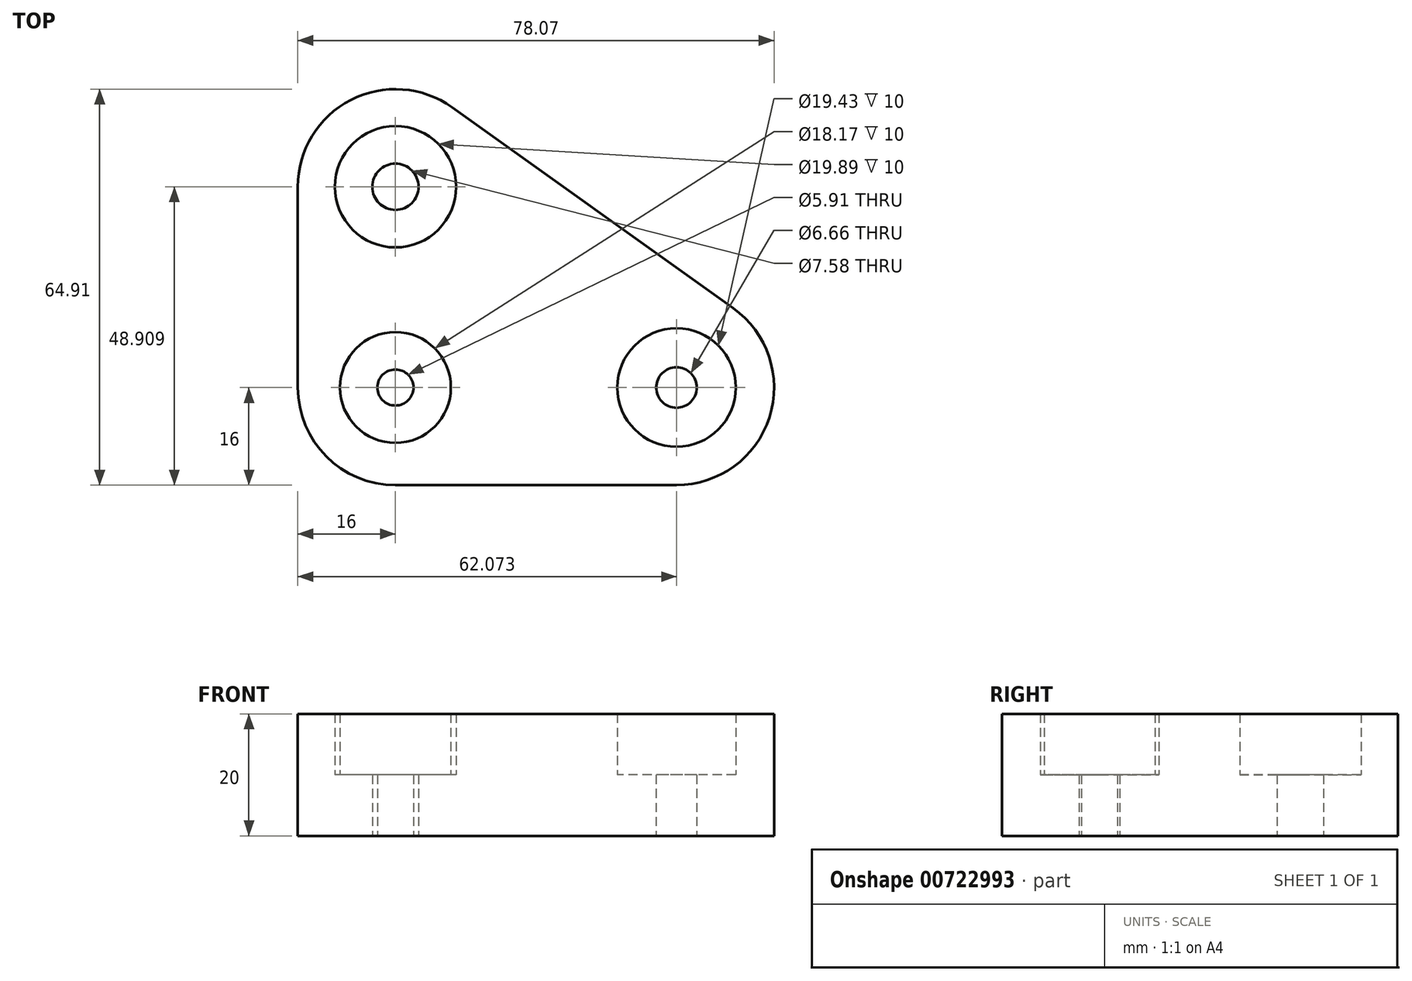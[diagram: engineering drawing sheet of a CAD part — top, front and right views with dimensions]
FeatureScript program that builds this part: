
annotation { "Feature Type Name" : "Feature", "Feature Type Description" : "" }
export const myFeature = defineFeature(function(context is Context, id is Id, definition is map)
    precondition{}
    {
        {
            var Q0;
            Q0=qCreatedBy(makeId("Top.planeOp"),FACE);
            var sketch = newSketch(context, id + "F0", { "sketchPlane" : qUnion([Q0])});
            skLineSegment(sketch, "E0.bottom", {"start": v(16, 0) * mm, "end": v(62.07, 0) * mm});
            skLineSegment(sketch, "E0.left", {"start": v(0, 16) * mm, "end": v(0, 48.9) * mm});
            skLineSegment(sketch, "E1", {"start": v(25.3, 61.93) * mm, "end": v(71.37, 29.02) * mm});
            skPoint(sketch, "E2.visualSharp", {"position": v(0, 0) * mm});
            skArc(sketch, "E2.filletArc", {"start": v(0, 16) * mm, "mid": v(4.69, 4.69) * mm, "end": v(16, 0) * mm});
            skPoint(sketch, "E3.visualSharp", {"position": v(0, 80) * mm});
            skArc(sketch, "E3.filletArc", {"start": v(25.3, 61.93) * mm, "mid": v(8.68, 63.14) * mm, "end": v(0, 48.9) * mm});
            skPoint(sketch, "E4.visualSharp", {"position": v(112, 0) * mm});
            skArc(sketch, "E4.filletArc", {"start": v(62.07, 0) * mm, "mid": v(77.3, 11.12) * mm, "end": v(71.37, 29.02) * mm});
            skCircle(sketch, "E5", {"center": v(16, 16) * mm, "radius": 9.09 * mm});
            skCircle(sketch, "E6", {"center": v(62.07, 16) * mm, "radius": 9.71 * mm});
            skCircle(sketch, "E7", {"center": v(16, 16) * mm, "radius": 2.96 * mm});
            skCircle(sketch, "E8", {"center": v(62.07, 16) * mm, "radius": 3.33 * mm});
            skCircle(sketch, "E9", {"center": v(16, 48.9) * mm, "radius": 9.94 * mm});
            skCircle(sketch, "E10", {"center": v(16, 48.9) * mm, "radius": 3.8 * mm});
            skSolve(sketch);
        }
        {
            var Q0;
            Q0 = qSketchRegion(id + "F0", true);
            extrude(context, id + "F1", {"entities" : qUnion([Q0]), "depth" : 20 * mm, "offsetDistance" : 25 * mm});
        }
        {
            var Q0;
            Q0=makeQuery(id+"F0.imprint","IMPRINT",FACE,{"disambiguationData":[TD([[makeQuery(id+"F0.imprint","IMPRINT",EDGE,{"derivedFrom":sQuery(id+"F0.wireOp",EDGE,"E5")}),1.0]])]});
            var Q1;
            Q1=makeQuery(id+"F0.imprint","IMPRINT",FACE,{"disambiguationData":[TD([[makeQuery(id+"F0.imprint","IMPRINT",EDGE,{"derivedFrom":sQuery(id+"F0.wireOp",EDGE,"E9")}),1.0]])]});
            var Q2;
            Q2=makeQuery(id+"F0.imprint","IMPRINT",FACE,{"disambiguationData":[TD([[makeQuery(id+"F0.imprint","IMPRINT",EDGE,{"derivedFrom":sQuery(id+"F0.wireOp",EDGE,"E6")}),1.0]])]});
            extrude(context, id + "F2", {"entities" : qUnion([Q0, Q1, Q2]), "operationType" : NewBodyOperationType.ADD, "depth" : 10 * mm, "offsetDistance" : 25 * mm});
        }
    });
